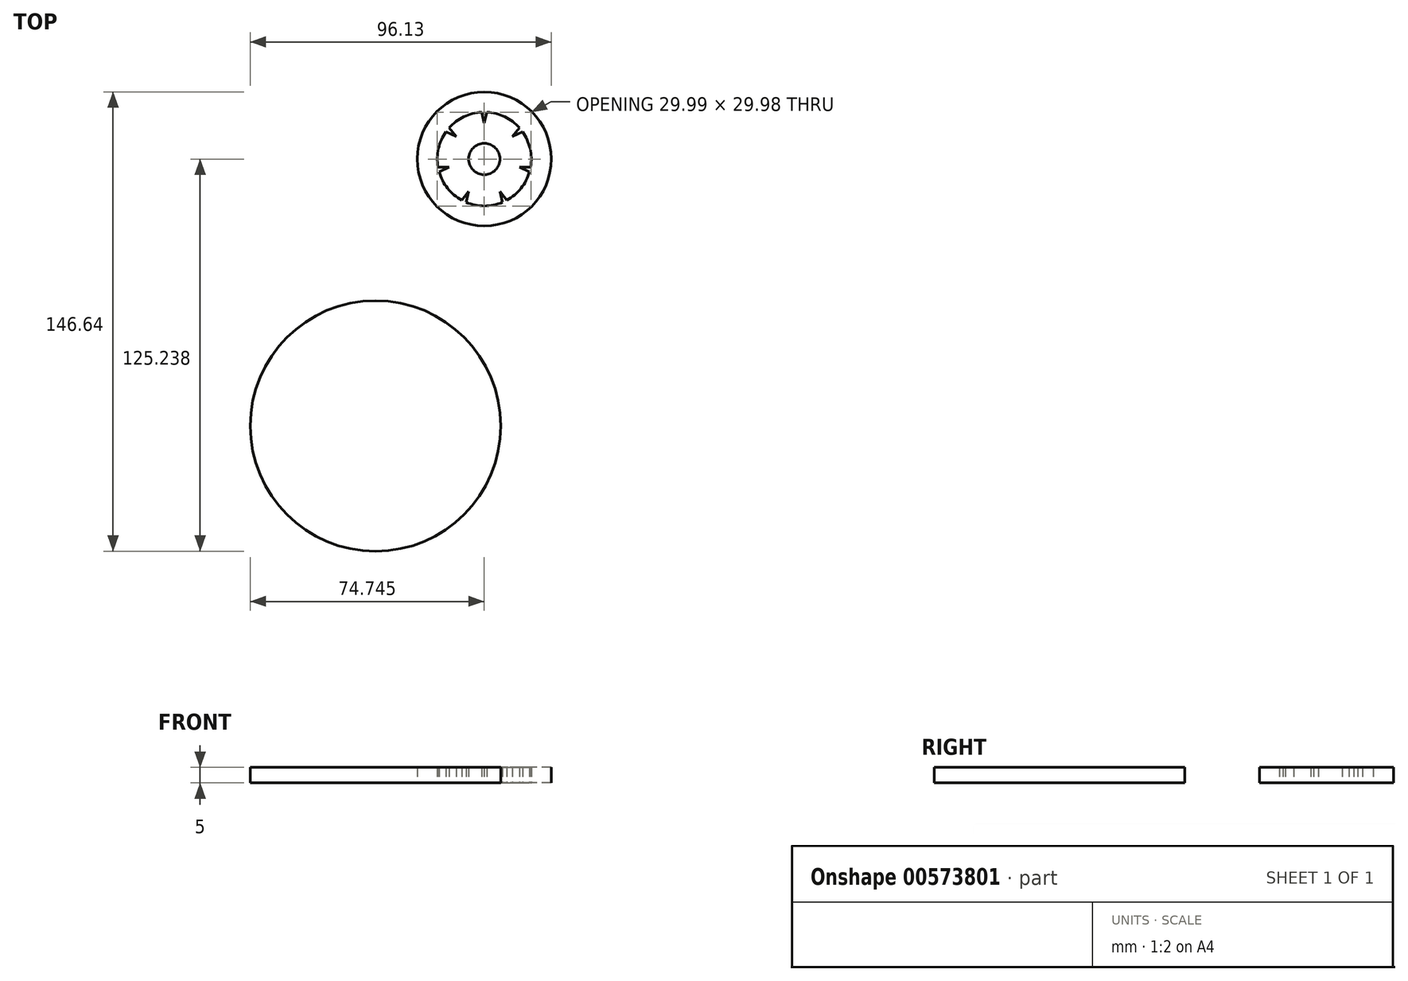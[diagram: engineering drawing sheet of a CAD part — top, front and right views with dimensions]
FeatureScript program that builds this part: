
annotation { "Feature Type Name" : "Feature", "Feature Type Description" : "" }
export const myFeature = defineFeature(function(context is Context, id is Id, definition is map)
    precondition{}
    {
        {
            var Q0;
            Q0=qCreatedBy(makeId("Top.planeOp"),FACE);
            var sketch = newSketch(context, id + "F0", { "sketchPlane" : qUnion([Q0])});
            skLineSegment(sketch, "E0.0", {"start": v(-11.35, 1.25) * mm, "end": v(-21.35, 1.25) * mm});
            skLineSegment(sketch, "E0.1", {"start": v(-21.35, 1.25) * mm, "end": v(-26.35, 9.91) * mm});
            skLineSegment(sketch, "E0.2", {"start": v(-26.35, 9.91) * mm, "end": v(-21.35, 18.57) * mm});
            skLineSegment(sketch, "E0.3", {"start": v(-21.35, 18.57) * mm, "end": v(-11.35, 18.57) * mm});
            skLineSegment(sketch, "E0.4", {"start": v(-11.35, 18.57) * mm, "end": v(-6.35, 9.91) * mm});
            skLineSegment(sketch, "E0.5", {"start": v(-6.35, 9.91) * mm, "end": v(-11.35, 1.25) * mm});
            skPoint(sketch, "E0.0.midPoint", {"position": v(-16.35, 1.25) * mm});
            skLineSegment(sketch, "E1", {"start": v(-21.35, 1.25) * mm, "end": v(-11.35, 1.25) * mm});
            skLineSegment(sketch, "E2", {"start": v(-11.35, 1.25) * mm, "end": v(-6.35, 9.91) * mm});
            skLineSegment(sketch, "E3", {"start": v(-6.35, 9.91) * mm, "end": v(-11.35, 18.57) * mm});
            skLineSegment(sketch, "E4", {"start": v(-11.35, 18.57) * mm, "end": v(-21.35, 18.57) * mm});
            skLineSegment(sketch, "E5", {"start": v(-21.35, 18.57) * mm, "end": v(-26.35, 9.91) * mm});
            skLineSegment(sketch, "E6", {"start": v(-26.35, 9.91) * mm, "end": v(-21.35, 1.25) * mm});
            skLineSegment(sketch, "E7.MirrorCS", {"start": v(-6.35, 27.23) * mm, "end": v(-11.35, 35.9) * mm});
            skLineSegment(sketch, "E8.MirrorCS", {"start": v(-21.35, 35.9) * mm, "end": v(-26.35, 27.23) * mm});
            skLineSegment(sketch, "E9.MirrorCS", {"start": v(-26.35, 27.23) * mm, "end": v(-21.35, 18.57) * mm});
            skLineSegment(sketch, "E10.MirrorCS", {"start": v(-11.35, 35.9) * mm, "end": v(-6.35, 27.23) * mm});
            skLineSegment(sketch, "E11.MirrorCS", {"start": v(-11.35, 35.9) * mm, "end": v(-21.35, 35.9) * mm});
            skLineSegment(sketch, "E12.MirrorCS", {"start": v(-11.35, 18.57) * mm, "end": v(-6.35, 27.23) * mm});
            skLineSegment(sketch, "E13.MirrorCS", {"start": v(-21.35, 35.9) * mm, "end": v(-11.35, 35.9) * mm});
            skLineSegment(sketch, "E14.MirrorCS", {"start": v(-6.35, 27.23) * mm, "end": v(-11.35, 18.57) * mm});
            skLineSegment(sketch, "E15.MirrorCS", {"start": v(-26.35, 27.23) * mm, "end": v(-21.35, 35.9) * mm});
            skLineSegment(sketch, "E16.MirrorCS", {"start": v(-21.35, 18.57) * mm, "end": v(-26.35, 27.23) * mm});
            skPoint(sketch, "E17.MirrorP", {"position": v(-16.35, 35.9) * mm});
            skLineSegment(sketch, "E18.MirrorCS", {"start": v(-6.35, 9.91) * mm, "end": v(3.65, 9.91) * mm});
            skLineSegment(sketch, "E19.MirrorCS", {"start": v(3.65, 9.91) * mm, "end": v(8.65, 18.57) * mm});
            skLineSegment(sketch, "E20.MirrorCS", {"start": v(8.65, 18.57) * mm, "end": v(3.65, 27.23) * mm});
            skLineSegment(sketch, "E21.MirrorCS", {"start": v(3.65, 27.23) * mm, "end": v(-6.35, 27.23) * mm});
            skLineSegment(sketch, "E22.MirrorCS", {"start": v(3.65, 9.91) * mm, "end": v(-6.35, 9.91) * mm});
            skPoint(sketch, "E23.MirrorP", {"position": v(6.15, 14.24) * mm});
            skLineSegment(sketch, "E24.MirrorCS", {"start": v(-6.35, 27.23) * mm, "end": v(3.65, 27.23) * mm});
            skLineSegment(sketch, "E25.MirrorCS", {"start": v(8.65, 18.57) * mm, "end": v(3.65, 9.91) * mm});
            skLineSegment(sketch, "E26.MirrorCS", {"start": v(3.65, 27.23) * mm, "end": v(8.65, 18.57) * mm});
            skLineSegment(sketch, "E27.MirrorCS", {"start": v(8.65, 1.25) * mm, "end": v(3.65, 9.91) * mm});
            skLineSegment(sketch, "E28.MirrorCS", {"start": v(3.65, -7.4) * mm, "end": v(8.65, 1.25) * mm});
            skLineSegment(sketch, "E29.MirrorCS", {"start": v(-6.35, -7.4) * mm, "end": v(3.65, -7.4) * mm});
            skLineSegment(sketch, "E30.MirrorCS", {"start": v(-11.35, 1.25) * mm, "end": v(-6.35, -7.4) * mm});
            skLineSegment(sketch, "E31.MirrorCS", {"start": v(3.65, 9.91) * mm, "end": v(8.65, 1.25) * mm});
            skPoint(sketch, "E32.MirrorP", {"position": v(-8.85, -3.08) * mm});
            skLineSegment(sketch, "E33.MirrorCS", {"start": v(3.65, -7.4) * mm, "end": v(-6.35, -7.4) * mm});
            skLineSegment(sketch, "E34.MirrorCS", {"start": v(-6.35, -7.4) * mm, "end": v(-11.35, 1.25) * mm});
            skLineSegment(sketch, "E35.MirrorCS", {"start": v(8.65, 1.25) * mm, "end": v(3.65, -7.4) * mm});
            skLineSegment(sketch, "E36.MirrorCS", {"start": v(-11.35, -16.07) * mm, "end": v(-6.35, -7.4) * mm});
            skLineSegment(sketch, "E37.MirrorCS", {"start": v(-6.35, -7.4) * mm, "end": v(-11.35, -16.07) * mm});
            skLineSegment(sketch, "E38.MirrorCS", {"start": v(-21.35, -16.07) * mm, "end": v(-11.35, -16.07) * mm});
            skLineSegment(sketch, "E39.MirrorCS", {"start": v(-21.35, 1.25) * mm, "end": v(-26.35, -7.4) * mm});
            skLineSegment(sketch, "E40.MirrorCS", {"start": v(-26.35, -7.4) * mm, "end": v(-21.35, -16.07) * mm});
            skLineSegment(sketch, "E41.MirrorCS", {"start": v(-11.35, -16.07) * mm, "end": v(-21.35, -16.07) * mm});
            skLineSegment(sketch, "E42.MirrorCS", {"start": v(-26.35, -7.4) * mm, "end": v(-21.35, 1.25) * mm});
            skLineSegment(sketch, "E43.MirrorCS", {"start": v(-21.35, -16.07) * mm, "end": v(-26.35, -7.4) * mm});
            skLineSegment(sketch, "E44.MirrorCS", {"start": v(-36.35, -7.4) * mm, "end": v(-26.35, -7.4) * mm});
            skLineSegment(sketch, "E45.MirrorCS", {"start": v(-41.35, 1.25) * mm, "end": v(-36.35, -7.4) * mm});
            skLineSegment(sketch, "E46.MirrorCS", {"start": v(-36.35, -7.4) * mm, "end": v(-41.35, 1.25) * mm});
            skLineSegment(sketch, "E47.MirrorCS", {"start": v(-26.35, -7.4) * mm, "end": v(-36.35, -7.4) * mm});
            skLineSegment(sketch, "E48.MirrorCS", {"start": v(-36.35, 9.91) * mm, "end": v(-41.35, 1.25) * mm});
            skLineSegment(sketch, "E49.MirrorCS", {"start": v(-41.35, 1.25) * mm, "end": v(-36.35, 9.91) * mm});
            skLineSegment(sketch, "E50.MirrorCS", {"start": v(-26.35, 9.91) * mm, "end": v(-36.35, 9.91) * mm});
            skLineSegment(sketch, "E51.MirrorCS", {"start": v(-36.35, 9.91) * mm, "end": v(-26.35, 9.91) * mm});
            skLineSegment(sketch, "E52.MirrorCS", {"start": v(-26.35, 27.23) * mm, "end": v(-36.35, 27.23) * mm});
            skLineSegment(sketch, "E53.MirrorCS", {"start": v(-36.35, 27.23) * mm, "end": v(-41.35, 18.57) * mm});
            skLineSegment(sketch, "E54.MirrorCS", {"start": v(-41.35, 18.57) * mm, "end": v(-36.35, 9.91) * mm});
            skLineSegment(sketch, "E55.MirrorCS", {"start": v(-41.35, 18.57) * mm, "end": v(-36.35, 27.23) * mm});
            skLineSegment(sketch, "E56.MirrorCS", {"start": v(-36.35, 27.23) * mm, "end": v(-26.35, 27.23) * mm});
            skPoint(sketch, "E57.MirrorP", {"position": v(-38.85, 14.24) * mm});
            skLineSegment(sketch, "E58.MirrorCS", {"start": v(-36.35, 9.91) * mm, "end": v(-41.35, 18.57) * mm});
            skLineSegment(sketch, "E59.MirrorCS", {"start": v(-26.35, 44.55) * mm, "end": v(-36.35, 44.55) * mm});
            skLineSegment(sketch, "E60.MirrorCS", {"start": v(-41.35, 35.9) * mm, "end": v(-36.35, 27.23) * mm});
            skLineSegment(sketch, "E61.MirrorCS", {"start": v(-36.35, 44.55) * mm, "end": v(-26.35, 44.55) * mm});
            skLineSegment(sketch, "E62.MirrorCS", {"start": v(-26.35, 44.55) * mm, "end": v(-21.35, 35.9) * mm});
            skLineSegment(sketch, "E63.MirrorCS", {"start": v(-36.35, 44.55) * mm, "end": v(-41.35, 35.9) * mm});
            skLineSegment(sketch, "E64.MirrorCS", {"start": v(-36.35, 27.23) * mm, "end": v(-41.35, 35.9) * mm});
            skLineSegment(sketch, "E65.MirrorCS", {"start": v(-21.35, 35.9) * mm, "end": v(-26.35, 44.55) * mm});
            skPoint(sketch, "E66.MirrorP", {"position": v(-38.85, 40.22) * mm});
            skLineSegment(sketch, "E67.MirrorCS", {"start": v(-41.35, 35.9) * mm, "end": v(-36.35, 44.55) * mm});
            skLineSegment(sketch, "E68.MirrorCS", {"start": v(-56.35, 9.91) * mm, "end": v(-51.35, 18.57) * mm});
            skLineSegment(sketch, "E69.MirrorCS", {"start": v(-41.35, 1.25) * mm, "end": v(-51.35, 1.25) * mm});
            skLineSegment(sketch, "E70.MirrorCS", {"start": v(-56.35, 9.91) * mm, "end": v(-51.35, 1.25) * mm});
            skLineSegment(sketch, "E71.MirrorCS", {"start": v(-51.35, 1.25) * mm, "end": v(-56.35, 9.91) * mm});
            skLineSegment(sketch, "E72.MirrorCS", {"start": v(-51.35, 18.57) * mm, "end": v(-56.35, 9.91) * mm});
            skLineSegment(sketch, "E73.MirrorCS", {"start": v(-51.35, 18.57) * mm, "end": v(-41.35, 18.57) * mm});
            skLineSegment(sketch, "E74.MirrorCS", {"start": v(-41.35, 18.57) * mm, "end": v(-51.35, 18.57) * mm});
            skLineSegment(sketch, "E75.MirrorCS", {"start": v(-51.35, 1.25) * mm, "end": v(-41.35, 1.25) * mm});
            skLineSegment(sketch, "E76.MirrorCS", {"start": v(-6.35, 44.55) * mm, "end": v(3.65, 44.55) * mm});
            skLineSegment(sketch, "E77.MirrorCS", {"start": v(3.65, 44.55) * mm, "end": v(-6.35, 44.55) * mm});
            skLineSegment(sketch, "E78.MirrorCS", {"start": v(8.65, 35.9) * mm, "end": v(3.65, 44.55) * mm});
            skLineSegment(sketch, "E79.MirrorCS", {"start": v(3.65, 44.55) * mm, "end": v(8.65, 35.9) * mm});
            skLineSegment(sketch, "E80.MirrorCS", {"start": v(8.65, 35.9) * mm, "end": v(3.65, 27.23) * mm});
            skLineSegment(sketch, "E81.MirrorCS", {"start": v(3.65, 27.23) * mm, "end": v(8.65, 35.9) * mm});
            skLineSegment(sketch, "E82.MirrorCS", {"start": v(-6.35, 44.55) * mm, "end": v(-11.35, 35.9) * mm});
            skLineSegment(sketch, "E83.MirrorCS", {"start": v(-11.35, 35.9) * mm, "end": v(-6.35, 44.55) * mm});
            skPoint(sketch, "E84.MirrorP", {"position": v(-8.85, 40.22) * mm});
            skLineSegment(sketch, "E85.MirrorCS", {"start": v(23.65, 9.91) * mm, "end": v(18.65, 18.57) * mm});
            skLineSegment(sketch, "E86.MirrorCS", {"start": v(18.65, 1.25) * mm, "end": v(23.65, 9.91) * mm});
            skLineSegment(sketch, "E87.MirrorCS", {"start": v(18.65, 18.57) * mm, "end": v(23.65, 9.91) * mm});
            skLineSegment(sketch, "E88.MirrorCS", {"start": v(23.65, 9.91) * mm, "end": v(18.65, 1.25) * mm});
            skLineSegment(sketch, "E89.MirrorCS", {"start": v(18.65, 1.25) * mm, "end": v(8.65, 1.25) * mm});
            skLineSegment(sketch, "E90.MirrorCS", {"start": v(18.65, 18.57) * mm, "end": v(8.65, 18.57) * mm});
            skLineSegment(sketch, "E91.MirrorCS", {"start": v(8.65, 1.25) * mm, "end": v(18.65, 1.25) * mm});
            skLineSegment(sketch, "E92.MirrorCS", {"start": v(8.65, 18.57) * mm, "end": v(18.65, 18.57) * mm});
            skLineSegment(sketch, "E93.MirrorCS", {"start": v(8.65, -16.07) * mm, "end": v(3.65, -24.73) * mm});
            skLineSegment(sketch, "E94.MirrorCS", {"start": v(3.65, -24.73) * mm, "end": v(8.65, -16.07) * mm});
            skLineSegment(sketch, "E95.MirrorCS", {"start": v(3.65, -24.73) * mm, "end": v(-6.35, -24.73) * mm});
            skLineSegment(sketch, "E96.MirrorCS", {"start": v(-6.35, -24.73) * mm, "end": v(3.65, -24.73) * mm});
            skLineSegment(sketch, "E97.MirrorCS", {"start": v(-6.35, -24.73) * mm, "end": v(-11.35, -16.07) * mm});
            skLineSegment(sketch, "E98.MirrorCS", {"start": v(-11.35, -16.07) * mm, "end": v(-6.35, -24.73) * mm});
            skPoint(sketch, "E99.MirrorP", {"position": v(-16.35, -16.07) * mm});
            skLineSegment(sketch, "E100.MirrorCS", {"start": v(8.65, -16.07) * mm, "end": v(3.65, -7.4) * mm});
            skPoint(sketch, "E101.MirrorP", {"position": v(-8.85, -11.74) * mm});
            skLineSegment(sketch, "E102.MirrorCS", {"start": v(3.65, -7.4) * mm, "end": v(8.65, -16.07) * mm});
            skLineSegment(sketch, "E103.MirrorCS", {"start": v(-26.35, -24.73) * mm, "end": v(-36.35, -24.73) * mm});
            skLineSegment(sketch, "E104.MirrorCS", {"start": v(-36.35, -24.73) * mm, "end": v(-26.35, -24.73) * mm});
            skLineSegment(sketch, "E105.MirrorCS", {"start": v(-36.35, -24.73) * mm, "end": v(-41.35, -16.07) * mm});
            skLineSegment(sketch, "E106.MirrorCS", {"start": v(-41.35, -16.07) * mm, "end": v(-36.35, -24.73) * mm});
            skLineSegment(sketch, "E107.MirrorCS", {"start": v(-41.35, -16.07) * mm, "end": v(-36.35, -7.4) * mm});
            skLineSegment(sketch, "E108.MirrorCS", {"start": v(-26.35, -24.73) * mm, "end": v(-21.35, -16.07) * mm});
            skPoint(sketch, "E109.MirrorP", {"position": v(-38.85, -11.74) * mm});
            skLineSegment(sketch, "E110.MirrorCS", {"start": v(-21.35, -16.07) * mm, "end": v(-26.35, -24.73) * mm});
            skPoint(sketch, "E111.MirrorP", {"position": v(-23.85, -20.4) * mm});
            skLineSegment(sketch, "E112.MirrorCS", {"start": v(-36.35, -7.4) * mm, "end": v(-41.35, -16.07) * mm});
            skPoint(sketch, "E113.MirrorP", {"position": v(-38.85, -20.4) * mm});
            skPoint(sketch, "E114.MirrorP", {"position": v(-31.35, -24.73) * mm});
            skLineSegment(sketch, "E115.0", {"start": v(107.66, 12.57) * mm, "end": v(97.66, 12.57) * mm});
            skLineSegment(sketch, "E115.1", {"start": v(97.66, 12.57) * mm, "end": v(91.43, 20.38) * mm});
            skLineSegment(sketch, "E115.2", {"start": v(91.43, 20.38) * mm, "end": v(93.66, 30.13) * mm});
            skLineSegment(sketch, "E115.3", {"start": v(93.66, 30.13) * mm, "end": v(102.66, 34.47) * mm});
            skLineSegment(sketch, "E115.4", {"start": v(102.66, 34.47) * mm, "end": v(111.67, 30.13) * mm});
            skLineSegment(sketch, "E115.5", {"start": v(111.67, 30.13) * mm, "end": v(113.9, 20.38) * mm});
            skLineSegment(sketch, "E115.6", {"start": v(113.9, 20.38) * mm, "end": v(107.66, 12.57) * mm});
            skPoint(sketch, "E115.0.midPoint", {"position": v(102.66, 12.57) * mm});
            skLineSegment(sketch, "E116", {"start": v(97.66, 12.57) * mm, "end": v(107.66, 12.57) * mm});
            skLineSegment(sketch, "E117", {"start": v(107.66, 12.57) * mm, "end": v(113.9, 20.38) * mm});
            skLineSegment(sketch, "E118", {"start": v(113.9, 20.38) * mm, "end": v(111.67, 30.13) * mm});
            skLineSegment(sketch, "E119", {"start": v(111.67, 30.13) * mm, "end": v(102.66, 34.47) * mm});
            skLineSegment(sketch, "E120", {"start": v(102.66, 34.47) * mm, "end": v(93.66, 30.13) * mm});
            skLineSegment(sketch, "E121", {"start": v(93.66, 30.13) * mm, "end": v(91.43, 20.38) * mm});
            skLineSegment(sketch, "E122", {"start": v(91.43, 20.38) * mm, "end": v(97.66, 12.57) * mm});
            skLineSegment(sketch, "E123.MirrorCS", {"start": v(106.67, 52.04) * mm, "end": v(116.67, 52.04) * mm});
            skLineSegment(sketch, "E124.MirrorCS", {"start": v(100.44, 44.22) * mm, "end": v(106.67, 52.04) * mm});
            skLineSegment(sketch, "E125.MirrorCS", {"start": v(116.67, 52.04) * mm, "end": v(122.9, 44.22) * mm});
            skLineSegment(sketch, "E126.MirrorCS", {"start": v(120.68, 34.47) * mm, "end": v(111.67, 30.13) * mm});
            skLineSegment(sketch, "E127.MirrorCS", {"start": v(122.9, 44.22) * mm, "end": v(120.68, 34.47) * mm});
            skLineSegment(sketch, "E128.MirrorCS", {"start": v(102.66, 34.47) * mm, "end": v(100.44, 44.22) * mm});
            skLineSegment(sketch, "E129.MirrorCS", {"start": v(116.67, 52.04) * mm, "end": v(106.67, 52.04) * mm});
            skLineSegment(sketch, "E130.MirrorCS", {"start": v(106.67, 52.04) * mm, "end": v(100.44, 44.22) * mm});
            skLineSegment(sketch, "E131.MirrorCS", {"start": v(100.44, 44.22) * mm, "end": v(102.66, 34.47) * mm});
            skLineSegment(sketch, "E132.MirrorCS", {"start": v(111.67, 30.13) * mm, "end": v(120.68, 34.47) * mm});
            skLineSegment(sketch, "E133.MirrorCS", {"start": v(122.9, 44.22) * mm, "end": v(116.67, 52.04) * mm});
            skLineSegment(sketch, "E134.MirrorCS", {"start": v(120.68, 34.47) * mm, "end": v(122.9, 44.22) * mm});
            skPoint(sketch, "E135.MirrorP", {"position": v(119.8, 48.13) * mm});
            skLineSegment(sketch, "E136.MirrorCS", {"start": v(111.67, 30.13) * mm, "end": v(117.9, 37.95) * mm});
            skLineSegment(sketch, "E137.MirrorCS", {"start": v(131.92, 20.38) * mm, "end": v(122.9, 16.05) * mm});
            skLineSegment(sketch, "E138.MirrorCS", {"start": v(134.14, 30.13) * mm, "end": v(131.92, 20.38) * mm});
            skLineSegment(sketch, "E139.MirrorCS", {"start": v(127.9, 37.95) * mm, "end": v(134.14, 30.13) * mm});
            skLineSegment(sketch, "E140.MirrorCS", {"start": v(122.9, 16.05) * mm, "end": v(113.9, 20.38) * mm});
            skLineSegment(sketch, "E141.MirrorCS", {"start": v(117.9, 37.95) * mm, "end": v(127.9, 37.95) * mm});
            skLineSegment(sketch, "E142.MirrorCS", {"start": v(131.92, 20.38) * mm, "end": v(134.14, 30.13) * mm});
            skLineSegment(sketch, "E143.MirrorCS", {"start": v(134.14, 30.13) * mm, "end": v(127.9, 37.95) * mm});
            skLineSegment(sketch, "E144.MirrorCS", {"start": v(127.9, 37.95) * mm, "end": v(117.9, 37.95) * mm});
            skPoint(sketch, "E145.MirrorP", {"position": v(127.41, 18.21) * mm});
            skLineSegment(sketch, "E146.MirrorCS", {"start": v(117.9, 37.95) * mm, "end": v(111.67, 30.13) * mm});
            skLineSegment(sketch, "E147.MirrorCS", {"start": v(113.9, 20.38) * mm, "end": v(122.9, 16.05) * mm});
            skLineSegment(sketch, "E148.MirrorCS", {"start": v(122.9, 16.05) * mm, "end": v(131.92, 20.38) * mm});
            skLineSegment(sketch, "E149.MirrorCS", {"start": v(123.9, 20.38) * mm, "end": v(130.13, 12.57) * mm});
            skLineSegment(sketch, "E150.MirrorCS", {"start": v(113.9, 20.38) * mm, "end": v(123.9, 20.38) * mm});
            skLineSegment(sketch, "E151.MirrorCS", {"start": v(127.9, 2.82) * mm, "end": v(118.9, -1.52) * mm});
            skLineSegment(sketch, "E152.MirrorCS", {"start": v(130.13, 12.57) * mm, "end": v(127.9, 2.82) * mm});
            skLineSegment(sketch, "E153.MirrorCS", {"start": v(109.89, 2.82) * mm, "end": v(107.66, 12.57) * mm});
            skLineSegment(sketch, "E154.MirrorCS", {"start": v(118.9, -1.52) * mm, "end": v(109.89, 2.82) * mm});
            skLineSegment(sketch, "E155.MirrorCS", {"start": v(107.66, 12.57) * mm, "end": v(109.89, 2.82) * mm});
            skPoint(sketch, "E156.MirrorP", {"position": v(108.78, 7.7) * mm});
            skLineSegment(sketch, "E157.MirrorCS", {"start": v(123.9, 20.38) * mm, "end": v(113.9, 20.38) * mm});
            skLineSegment(sketch, "E158.MirrorCS", {"start": v(127.9, 2.82) * mm, "end": v(130.13, 12.57) * mm});
            skLineSegment(sketch, "E159.MirrorCS", {"start": v(109.89, 2.82) * mm, "end": v(118.9, -1.52) * mm});
            skLineSegment(sketch, "E160.MirrorCS", {"start": v(130.13, 12.57) * mm, "end": v(123.9, 20.38) * mm});
            skLineSegment(sketch, "E161.MirrorCS", {"start": v(118.9, -1.52) * mm, "end": v(127.9, 2.82) * mm});
            skLineSegment(sketch, "E162.MirrorCS", {"start": v(107.66, 12.57) * mm, "end": v(113.9, 4.75) * mm});
            skLineSegment(sketch, "E163.MirrorCS", {"start": v(111.67, -5) * mm, "end": v(102.66, -9.34) * mm});
            skLineSegment(sketch, "E164.MirrorCS", {"start": v(113.9, 4.75) * mm, "end": v(111.67, -5) * mm});
            skLineSegment(sketch, "E165.MirrorCS", {"start": v(91.43, 4.75) * mm, "end": v(97.66, 12.57) * mm});
            skLineSegment(sketch, "E166.MirrorCS", {"start": v(93.66, -5) * mm, "end": v(91.43, 4.75) * mm});
            skLineSegment(sketch, "E167.MirrorCS", {"start": v(102.66, -9.34) * mm, "end": v(93.66, -5) * mm});
            skLineSegment(sketch, "E168.MirrorCS", {"start": v(97.66, 12.57) * mm, "end": v(91.43, 4.75) * mm});
            skLineSegment(sketch, "E169.MirrorCS", {"start": v(91.43, 4.75) * mm, "end": v(93.66, -5) * mm});
            skLineSegment(sketch, "E170.MirrorCS", {"start": v(93.66, -5) * mm, "end": v(102.66, -9.34) * mm});
            skLineSegment(sketch, "E171.MirrorCS", {"start": v(102.66, -9.34) * mm, "end": v(111.67, -5) * mm});
            skLineSegment(sketch, "E172.MirrorCS", {"start": v(111.67, -5) * mm, "end": v(113.9, 4.75) * mm});
            skLineSegment(sketch, "E173.MirrorCS", {"start": v(113.9, 4.75) * mm, "end": v(107.66, 12.57) * mm});
            skLineSegment(sketch, "E174.MirrorCS", {"start": v(97.66, 12.57) * mm, "end": v(95.44, 2.82) * mm});
            skLineSegment(sketch, "E175.MirrorCS", {"start": v(77.42, 2.82) * mm, "end": v(75.2, 12.57) * mm});
            skLineSegment(sketch, "E176.MirrorCS", {"start": v(86.43, -1.52) * mm, "end": v(77.42, 2.82) * mm});
            skLineSegment(sketch, "E177.MirrorCS", {"start": v(95.44, 2.82) * mm, "end": v(86.43, -1.52) * mm});
            skLineSegment(sketch, "E178.MirrorCS", {"start": v(81.43, 20.38) * mm, "end": v(91.43, 20.38) * mm});
            skLineSegment(sketch, "E179.MirrorCS", {"start": v(75.2, 12.57) * mm, "end": v(81.43, 20.38) * mm});
            skPoint(sketch, "E180.MirrorP", {"position": v(96.55, 7.7) * mm});
            skLineSegment(sketch, "E181.MirrorCS", {"start": v(86.43, -1.52) * mm, "end": v(95.44, 2.82) * mm});
            skLineSegment(sketch, "E182.MirrorCS", {"start": v(77.42, 2.82) * mm, "end": v(86.43, -1.52) * mm});
            skLineSegment(sketch, "E183.MirrorCS", {"start": v(95.44, 2.82) * mm, "end": v(97.66, 12.57) * mm});
            skLineSegment(sketch, "E184.MirrorCS", {"start": v(75.2, 12.57) * mm, "end": v(77.42, 2.82) * mm});
            skLineSegment(sketch, "E185.MirrorCS", {"start": v(81.43, 20.38) * mm, "end": v(75.2, 12.57) * mm});
            skLineSegment(sketch, "E186.MirrorCS", {"start": v(91.43, 20.38) * mm, "end": v(81.43, 20.38) * mm});
            skLineSegment(sketch, "E187.MirrorCS", {"start": v(82.42, 44.22) * mm, "end": v(88.66, 52.04) * mm});
            skLineSegment(sketch, "E188.MirrorCS", {"start": v(88.66, 52.04) * mm, "end": v(98.66, 52.04) * mm});
            skLineSegment(sketch, "E189.MirrorCS", {"start": v(84.65, 34.47) * mm, "end": v(82.42, 44.22) * mm});
            skLineSegment(sketch, "E190.MirrorCS", {"start": v(104.89, 44.22) * mm, "end": v(102.66, 34.47) * mm});
            skLineSegment(sketch, "E191.MirrorCS", {"start": v(98.66, 52.04) * mm, "end": v(104.89, 44.22) * mm});
            skLineSegment(sketch, "E192.MirrorCS", {"start": v(82.42, 44.22) * mm, "end": v(84.65, 34.47) * mm});
            skPoint(sketch, "E193.MirrorP", {"position": v(85.54, 48.13) * mm});
            skLineSegment(sketch, "E194.MirrorCS", {"start": v(93.66, 30.13) * mm, "end": v(84.65, 34.47) * mm});
            skLineSegment(sketch, "E195.MirrorCS", {"start": v(98.66, 52.04) * mm, "end": v(88.66, 52.04) * mm});
            skLineSegment(sketch, "E196.MirrorCS", {"start": v(84.65, 34.47) * mm, "end": v(93.66, 30.13) * mm});
            skLineSegment(sketch, "E197.MirrorCS", {"start": v(104.89, 44.22) * mm, "end": v(98.66, 52.04) * mm});
            skLineSegment(sketch, "E198.MirrorCS", {"start": v(102.66, 34.47) * mm, "end": v(104.89, 44.22) * mm});
            skLineSegment(sketch, "E199.MirrorCS", {"start": v(88.66, 52.04) * mm, "end": v(82.42, 44.22) * mm});
            skLineSegment(sketch, "E200.MirrorCS", {"start": v(82.42, 16.05) * mm, "end": v(73.41, 20.38) * mm});
            skLineSegment(sketch, "E201.MirrorCS", {"start": v(73.41, 20.38) * mm, "end": v(82.42, 16.05) * mm});
            skLineSegment(sketch, "E202.MirrorCS", {"start": v(87.42, 37.95) * mm, "end": v(93.66, 30.13) * mm});
            skLineSegment(sketch, "E203.MirrorCS", {"start": v(77.42, 37.95) * mm, "end": v(87.42, 37.95) * mm});
            skLineSegment(sketch, "E204.MirrorCS", {"start": v(71.19, 30.13) * mm, "end": v(77.42, 37.95) * mm});
            skLineSegment(sketch, "E205.MirrorCS", {"start": v(73.41, 20.38) * mm, "end": v(71.19, 30.13) * mm});
            skLineSegment(sketch, "E206.MirrorCS", {"start": v(91.43, 20.38) * mm, "end": v(82.42, 16.05) * mm});
            skLineSegment(sketch, "E207.MirrorCS", {"start": v(82.42, 16.05) * mm, "end": v(91.43, 20.38) * mm});
            skPoint(sketch, "E208.MirrorP", {"position": v(77.92, 18.21) * mm});
            skLineSegment(sketch, "E209.MirrorCS", {"start": v(93.66, 30.13) * mm, "end": v(87.42, 37.95) * mm});
            skLineSegment(sketch, "E210.MirrorCS", {"start": v(71.19, 30.13) * mm, "end": v(73.41, 20.38) * mm});
            skLineSegment(sketch, "E211.MirrorCS", {"start": v(77.42, 37.95) * mm, "end": v(71.19, 30.13) * mm});
            skLineSegment(sketch, "E212.MirrorCS", {"start": v(87.42, 37.95) * mm, "end": v(77.42, 37.95) * mm});
            skCircle(sketch, "E213", {"center": v(67.92, -62.3) * mm, "radius": 40 * mm});
            skLineSegment(sketch, "E214", {"start": v(93.66, 30.13) * mm, "end": v(110.78, 16.47) * mm});
            skLineSegment(sketch, "E215", {"start": v(107.66, 12.57) * mm, "end": v(98.16, 32.3) * mm});
            skLineSegment(sketch, "E216", {"start": v(91.43, 20.38) * mm, "end": v(112.79, 25.26) * mm});
            skLineSegment(sketch, "E217", {"start": v(97.66, 12.57) * mm, "end": v(107.17, 32.3) * mm});
            skLineSegment(sketch, "E218", {"start": v(111.67, 30.13) * mm, "end": v(94.55, 16.47) * mm});
            skLineSegment(sketch, "E219", {"start": v(113.9, 20.38) * mm, "end": v(92.54, 25.26) * mm});
            skLineSegment(sketch, "E220", {"start": v(102.66, 34.47) * mm, "end": v(102.66, 12.57) * mm});
            skCircle(sketch, "E221", {"center": v(102.66, 22.95) * mm, "radius": 15 * mm});
            skCircle(sketch, "E222", {"center": v(102.66, 22.95) * mm, "radius": 21.39 * mm});
            skCircle(sketch, "E223", {"center": v(102.66, 22.95) * mm, "radius": 29.37 * mm});
            skCircle(sketch, "E224", {"center": v(102.66, 22.95) * mm, "radius": 5 * mm});
            skSolve(sketch);
        }
        {
            var Q0;
            Q0=makeQuery(id+"F0.imprint","IMPRINT",FACE,{"disambiguationData":[TD([[makeQuery(id+"F0.imprint","IMPRINT",EDGE,{"derivedFrom":sQuery(id+"F0.wireOp",EDGE,"E213")}),1.0]])]});
            var Q1;
            {var subQ0=sQuery(id+"F0.wireOp",EDGE,"E129.MirrorCS");Q1=makeQuery(id+"F0.imprint","IMPRINT",FACE,{"disambiguationData":[TD([[makeQuery(id+"F0.imprint","IMPRINT",EDGE,{"derivedFrom":subQ0}),1.0]])]});}
            var Q2;
            {var subQ0=sQuery(id+"F0.wireOp",EDGE,"E142.MirrorCS");Q2=makeQuery(id+"F0.imprint","IMPRINT",FACE,{"disambiguationData":[TD([[makeQuery(id+"F0.imprint","IMPRINT",EDGE,{"derivedFrom":subQ0}),1.0]])]});}
            var Q3;
            {var subQ0=sQuery(id+"F0.wireOp",EDGE,"E158.MirrorCS");Q3=makeQuery(id+"F0.imprint","IMPRINT",FACE,{"disambiguationData":[TD([[makeQuery(id+"F0.imprint","IMPRINT",EDGE,{"derivedFrom":subQ0}),1.0]])]});}
            var Q4;
            {var subQ0=sQuery(id+"F0.wireOp",EDGE,"E170.MirrorCS");Q4=makeQuery(id+"F0.imprint","IMPRINT",FACE,{"disambiguationData":[TD([[makeQuery(id+"F0.imprint","IMPRINT",EDGE,{"derivedFrom":subQ0}),1.0]])]});}
            var Q5;
            {var subQ0=sQuery(id+"F0.wireOp",EDGE,"E182.MirrorCS");Q5=makeQuery(id+"F0.imprint","IMPRINT",FACE,{"disambiguationData":[TD([[makeQuery(id+"F0.imprint","IMPRINT",EDGE,{"derivedFrom":subQ0}),1.0]])]});}
            var Q6;
            {var subQ0=sQuery(id+"F0.wireOp",EDGE,"E195.MirrorCS");Q6=makeQuery(id+"F0.imprint","IMPRINT",FACE,{"disambiguationData":[TD([[makeQuery(id+"F0.imprint","IMPRINT",EDGE,{"derivedFrom":subQ0}),1.0]])]});}
            var Q7;
            {var subQ0=sQuery(id+"F0.wireOp",EDGE,"E210.MirrorCS");Q7=makeQuery(id+"F0.imprint","IMPRINT",FACE,{"disambiguationData":[TD([[makeQuery(id+"F0.imprint","IMPRINT",EDGE,{"derivedFrom":subQ0}),1.0]])]});}
            var Q8;
            Q8=makeQuery(id+"F0.imprint","IMPRINT",FACE,{"disambiguationData":[TD([[makeQuery(id+"F0.imprint","IMPRINT",EDGE,{"derivedFrom":sQuery(id+"F0.wireOp",EDGE,"E52.MirrorCS")}),-1.0]])]});
            var Q9;
            Q9=makeQuery(id+"F0.imprint","IMPRINT",FACE,{"disambiguationData":[TD([[makeQuery(id+"F0.imprint","IMPRINT",EDGE,{"derivedFrom":sQuery(id+"F0.wireOp",EDGE,"E49.MirrorCS")}),1.0]])]});
            var Q10;
            Q10=makeQuery(id+"F0.imprint","IMPRINT",FACE,{"disambiguationData":[TD([[makeQuery(id+"F0.imprint","IMPRINT",EDGE,{"derivedFrom":sQuery(id+"F0.wireOp",EDGE,"E7.MirrorCS")}),-1.0]])]});
            var Q11;
            Q11=makeQuery(id+"F0.imprint","IMPRINT",FACE,{"disambiguationData":[TD([[makeQuery(id+"F0.imprint","IMPRINT",EDGE,{"derivedFrom":sQuery(id+"F0.wireOp",EDGE,"E19.MirrorCS")}),-1.0]])]});
            var Q12;
            Q12=makeQuery(id+"F0.imprint","IMPRINT",FACE,{"disambiguationData":[TD([[makeQuery(id+"F0.imprint","IMPRINT",EDGE,{"derivedFrom":sQuery(id+"F0.wireOp",EDGE,"E33.MirrorCS")}),1.0]])]});
            var Q13;
            Q13=makeQuery(id+"F0.imprint","IMPRINT",FACE,{"disambiguationData":[TD([[makeQuery(id+"F0.imprint","IMPRINT",EDGE,{"derivedFrom":sQuery(id+"F0.wireOp",EDGE,"E104.MirrorCS")}),1.0]])]});
            var Q14;
            Q14=makeQuery(id+"F0.imprint","IMPRINT",FACE,{"disambiguationData":[TD([[makeQuery(id+"F0.imprint","IMPRINT",EDGE,{"derivedFrom":sQuery(id+"F0.wireOp",EDGE,"E0.3")}),1.0]])]});
            var Q15;
            Q15=makeQuery(id+"F0.imprint","IMPRINT",FACE,{"disambiguationData":[TD([[makeQuery(id+"F0.imprint","IMPRINT",EDGE,{"derivedFrom":sQuery(id+"F0.wireOp",EDGE,"E0.4")}),1.0]])]});
            var Q16;
            Q16=makeQuery(id+"F0.imprint","IMPRINT",FACE,{"disambiguationData":[TD([[makeQuery(id+"F0.imprint","IMPRINT",EDGE,{"derivedFrom":sQuery(id+"F0.wireOp",EDGE,"E2")}),-1.0]])]});
            var Q17;
            Q17=makeQuery(id+"F0.imprint","IMPRINT",FACE,{"disambiguationData":[TD([[makeQuery(id+"F0.imprint","IMPRINT",EDGE,{"derivedFrom":sQuery(id+"F0.wireOp",EDGE,"E0.0")}),1.0]])]});
            var Q18;
            Q18=makeQuery(id+"F0.imprint","IMPRINT",FACE,{"disambiguationData":[TD([[makeQuery(id+"F0.imprint","IMPRINT",EDGE,{"derivedFrom":sQuery(id+"F0.wireOp",EDGE,"E0.1")}),1.0]])]});
            var Q19;
            Q19=makeQuery(id+"F0.imprint","IMPRINT",FACE,{"disambiguationData":[TD([[makeQuery(id+"F0.imprint","IMPRINT",EDGE,{"derivedFrom":sQuery(id+"F0.wireOp",EDGE,"E0.2")}),1.0]])]});
            var Q20;
            {var subQ1=sQuery(id+"F0.wireOp",EDGE,"E197.MirrorCS");var subQ3=sQuery(id+"F0.wireOp",EDGE,"E130.MirrorCS");var subQ4=makeQuery(id+"F0.imprint","INTERSECT",VERTEX,{"derivedFrom":[subQ3,subQ1]});Q20=makeQuery(id+"F0.imprint","IMPRINT",FACE,{"disambiguationData":[TD([[makeQuery(id+"F0.imprint","IMPRINT",EDGE,{"disambiguationData":[TD([[subQ4,1.0]])],"derivedFrom":subQ3}),1.0]])]});}
            var Q21;
            {var subQ6=sQuery(id+"F0.wireOp",EDGE,"E197.MirrorCS");var subQ8=sQuery(id+"F0.wireOp",EDGE,"E130.MirrorCS");var subQ9=makeQuery(id+"F0.imprint","INTERSECT",VERTEX,{"derivedFrom":[subQ8,subQ6]});Q21=makeQuery(id+"F0.imprint","IMPRINT",FACE,{"disambiguationData":[TD([[makeQuery(id+"F0.imprint","IMPRINT",EDGE,{"disambiguationData":[TD([[subQ9,-1.0]])],"derivedFrom":subQ8}),-1.0]])]});}
            var Q22;
            {var subQ7=sQuery(id+"F0.wireOp",EDGE,"E144.MirrorCS");var subQ9=sQuery(id+"F0.wireOp",EDGE,"E134.MirrorCS");var subQ10=makeQuery(id+"F0.imprint","INTERSECT",VERTEX,{"derivedFrom":[subQ9,subQ7]});Q22=makeQuery(id+"F0.imprint","IMPRINT",FACE,{"disambiguationData":[TD([[makeQuery(id+"F0.imprint","IMPRINT",EDGE,{"disambiguationData":[TD([[subQ10,1.0]])],"derivedFrom":subQ9}),-1.0]])]});}
            var Q23;
            {var subQ6=sQuery(id+"F0.wireOp",EDGE,"E160.MirrorCS");var subQ8=sQuery(id+"F0.wireOp",EDGE,"E148.MirrorCS");var subQ9=makeQuery(id+"F0.imprint","INTERSECT",VERTEX,{"derivedFrom":[subQ8,subQ6]});Q23=makeQuery(id+"F0.imprint","IMPRINT",FACE,{"disambiguationData":[TD([[makeQuery(id+"F0.imprint","IMPRINT",EDGE,{"disambiguationData":[TD([[subQ9,1.0]])],"derivedFrom":subQ8}),-1.0]])]});}
            var Q24;
            {var subQ1=sQuery(id+"F0.wireOp",EDGE,"E172.MirrorCS");var subQ3=sQuery(id+"F0.wireOp",EDGE,"E159.MirrorCS");var subQ4=makeQuery(id+"F0.imprint","INTERSECT",VERTEX,{"derivedFrom":[subQ3,subQ1]});Q24=makeQuery(id+"F0.imprint","IMPRINT",FACE,{"disambiguationData":[TD([[makeQuery(id+"F0.imprint","IMPRINT",EDGE,{"disambiguationData":[TD([[subQ4,1.0]])],"derivedFrom":subQ3}),-1.0]])]});}
            var Q25;
            {var subQ5=sQuery(id+"F0.wireOp",EDGE,"E169.MirrorCS");var subQ7=sQuery(id+"F0.wireOp",EDGE,"E181.MirrorCS");var subQ8=makeQuery(id+"F0.imprint","INTERSECT",VERTEX,{"derivedFrom":[subQ5,subQ7]});Q25=makeQuery(id+"F0.imprint","IMPRINT",FACE,{"disambiguationData":[TD([[makeQuery(id+"F0.imprint","IMPRINT",EDGE,{"disambiguationData":[TD([[subQ8,1.0]])],"derivedFrom":subQ5}),-1.0]])]});}
            var Q26;
            {var subQ1=sQuery(id+"F0.wireOp",EDGE,"E201.MirrorCS");var subQ3=sQuery(id+"F0.wireOp",EDGE,"E185.MirrorCS");var subQ4=makeQuery(id+"F0.imprint","INTERSECT",VERTEX,{"derivedFrom":[subQ3,subQ1]});Q26=makeQuery(id+"F0.imprint","IMPRINT",FACE,{"disambiguationData":[TD([[makeQuery(id+"F0.imprint","IMPRINT",EDGE,{"disambiguationData":[TD([[subQ4,1.0]])],"derivedFrom":subQ3}),-1.0]])]});}
            var Q27;
            {var subQ1=sQuery(id+"F0.wireOp",EDGE,"E146.MirrorCS");var subQ3=sQuery(id+"F0.wireOp",EDGE,"E221");var subQ4=makeQuery(id+"F0.imprint","INTERSECT",VERTEX,{"derivedFrom":[subQ1,subQ3]});Q27=makeQuery(id+"F0.imprint","IMPRINT",FACE,{"disambiguationData":[TD([[makeQuery(id+"F0.imprint","IMPRINT",EDGE,{"disambiguationData":[TD([[subQ4,-1.0]])],"derivedFrom":subQ3}),-1.0]])]});}
            var Q28;
            {var subQ3=sQuery(id+"F0.wireOp",EDGE,"E221");var subQ5=sQuery(id+"F0.wireOp",EDGE,"E146.MirrorCS");var subQ7=makeQuery(id+"F0.imprint","INTERSECT",VERTEX,{"derivedFrom":[subQ5,subQ3]});Q28=makeQuery(id+"F0.imprint","IMPRINT",FACE,{"disambiguationData":[TD([[makeQuery(id+"F0.imprint","IMPRINT",EDGE,{"disambiguationData":[TD([[subQ7,-1.0]])],"derivedFrom":subQ3}),1.0]])]});}
            var Q29;
            {var subQ1=sQuery(id+"F0.wireOp",EDGE,"E132.MirrorCS");var subQ3=sQuery(id+"F0.wireOp",EDGE,"E221");var subQ4=makeQuery(id+"F0.imprint","INTERSECT",VERTEX,{"derivedFrom":[subQ1,subQ3]});Q29=makeQuery(id+"F0.imprint","IMPRINT",FACE,{"disambiguationData":[TD([[makeQuery(id+"F0.imprint","IMPRINT",EDGE,{"disambiguationData":[TD([[subQ4,1.0]])],"derivedFrom":subQ3}),-1.0]])]});}
            var Q30;
            {var subQ3=sQuery(id+"F0.wireOp",EDGE,"E221");var subQ5=sQuery(id+"F0.wireOp",EDGE,"E132.MirrorCS");var subQ8=makeQuery(id+"F0.imprint","INTERSECT",VERTEX,{"derivedFrom":[subQ5,subQ3]});Q30=makeQuery(id+"F0.imprint","IMPRINT",FACE,{"disambiguationData":[TD([[makeQuery(id+"F0.imprint","IMPRINT",EDGE,{"disambiguationData":[TD([[subQ8,1.0]])],"derivedFrom":subQ3}),1.0]])]});}
            var Q31;
            {var subQ1=sQuery(id+"F0.wireOp",EDGE,"E147.MirrorCS");var subQ3=sQuery(id+"F0.wireOp",EDGE,"E221");var subQ4=makeQuery(id+"F0.imprint","INTERSECT",VERTEX,{"derivedFrom":[subQ1,subQ3]});Q31=makeQuery(id+"F0.imprint","IMPRINT",FACE,{"disambiguationData":[TD([[makeQuery(id+"F0.imprint","IMPRINT",EDGE,{"disambiguationData":[TD([[subQ4,1.0]])],"derivedFrom":subQ3}),-1.0]])]});}
            var Q32;
            {var subQ3=sQuery(id+"F0.wireOp",EDGE,"E221");var subQ5=sQuery(id+"F0.wireOp",EDGE,"E147.MirrorCS");var subQ8=makeQuery(id+"F0.imprint","INTERSECT",VERTEX,{"derivedFrom":[subQ5,subQ3]});Q32=makeQuery(id+"F0.imprint","IMPRINT",FACE,{"disambiguationData":[TD([[makeQuery(id+"F0.imprint","IMPRINT",EDGE,{"disambiguationData":[TD([[subQ8,1.0]])],"derivedFrom":subQ3}),1.0]])]});}
            var Q33;
            {var subQ3=sQuery(id+"F0.wireOp",EDGE,"E221");var subQ5=sQuery(id+"F0.wireOp",EDGE,"E155.MirrorCS");var subQ8=makeQuery(id+"F0.imprint","INTERSECT",VERTEX,{"derivedFrom":[subQ5,subQ3]});Q33=makeQuery(id+"F0.imprint","IMPRINT",FACE,{"disambiguationData":[TD([[makeQuery(id+"F0.imprint","IMPRINT",EDGE,{"disambiguationData":[TD([[subQ8,1.0]])],"derivedFrom":subQ3}),1.0]])]});}
            var Q34;
            {var subQ1=sQuery(id+"F0.wireOp",EDGE,"E186.MirrorCS");var subQ3=sQuery(id+"F0.wireOp",EDGE,"E221");var subQ4=makeQuery(id+"F0.imprint","INTERSECT",VERTEX,{"derivedFrom":[subQ1,subQ3]});Q34=makeQuery(id+"F0.imprint","IMPRINT",FACE,{"disambiguationData":[TD([[makeQuery(id+"F0.imprint","IMPRINT",EDGE,{"disambiguationData":[TD([[subQ4,1.0]])],"derivedFrom":subQ3}),-1.0]])]});}
            var Q35;
            {var subQ1=sQuery(id+"F0.wireOp",EDGE,"E186.MirrorCS");var subQ6=sQuery(id+"F0.wireOp",EDGE,"E221");var subQ8=makeQuery(id+"F0.imprint","INTERSECT",VERTEX,{"derivedFrom":[subQ1,subQ6]});Q35=makeQuery(id+"F0.imprint","IMPRINT",FACE,{"disambiguationData":[TD([[makeQuery(id+"F0.imprint","IMPRINT",EDGE,{"disambiguationData":[TD([[subQ8,1.0]])],"derivedFrom":subQ6}),1.0]])]});}
            var Q36;
            {var subQ1=sQuery(id+"F0.wireOp",EDGE,"E131.MirrorCS");var subQ3=sQuery(id+"F0.wireOp",EDGE,"E221");var subQ4=makeQuery(id+"F0.imprint","INTERSECT",VERTEX,{"derivedFrom":[subQ1,subQ3]});Q36=makeQuery(id+"F0.imprint","IMPRINT",FACE,{"disambiguationData":[TD([[makeQuery(id+"F0.imprint","IMPRINT",EDGE,{"disambiguationData":[TD([[subQ4,-1.0]])],"derivedFrom":subQ3}),-1.0]])]});}
            var Q37;
            {var subQ3=sQuery(id+"F0.wireOp",EDGE,"E221");var subQ5=sQuery(id+"F0.wireOp",EDGE,"E131.MirrorCS");var subQ8=makeQuery(id+"F0.imprint","INTERSECT",VERTEX,{"derivedFrom":[subQ5,subQ3]});Q37=makeQuery(id+"F0.imprint","IMPRINT",FACE,{"disambiguationData":[TD([[makeQuery(id+"F0.imprint","IMPRINT",EDGE,{"disambiguationData":[TD([[subQ8,-1.0]])],"derivedFrom":subQ3}),1.0]])]});}
            var Q38;
            {var subQ1=sQuery(id+"F0.wireOp",EDGE,"E155.MirrorCS");var subQ3=sQuery(id+"F0.wireOp",EDGE,"E221");var subQ4=makeQuery(id+"F0.imprint","INTERSECT",VERTEX,{"derivedFrom":[subQ1,subQ3]});Q38=makeQuery(id+"F0.imprint","IMPRINT",FACE,{"disambiguationData":[TD([[makeQuery(id+"F0.imprint","IMPRINT",EDGE,{"disambiguationData":[TD([[subQ4,1.0]])],"derivedFrom":subQ3}),-1.0]])]});}
            var Q39;
            {var subQ1=sQuery(id+"F0.wireOp",EDGE,"E168.MirrorCS");var subQ3=sQuery(id+"F0.wireOp",EDGE,"E221");var subQ4=makeQuery(id+"F0.imprint","INTERSECT",VERTEX,{"derivedFrom":[subQ1,subQ3]});Q39=makeQuery(id+"F0.imprint","IMPRINT",FACE,{"disambiguationData":[TD([[makeQuery(id+"F0.imprint","IMPRINT",EDGE,{"disambiguationData":[TD([[subQ4,1.0]])],"derivedFrom":subQ3}),-1.0]])]});}
            var Q40;
            {var subQ0=sQuery(id+"F0.wireOp",EDGE,"E224");var subQ1=sQuery(id+"F0.wireOp",EDGE,"E217");var subQ2=makeQuery(id+"F0.imprint","INTERSECT",VERTEX,{"disambiguationData":[OD(0.0)],"derivedFrom":[subQ1,subQ0]});Q40=makeQuery(id+"F0.imprint","IMPRINT",FACE,{"disambiguationData":[TD([[makeQuery(id+"F0.imprint","IMPRINT",EDGE,{"disambiguationData":[TD([[subQ2,-1.0]])],"derivedFrom":subQ0}),1.0]])]});}
            var Q41;
            {var subQ0=sQuery(id+"F0.wireOp",EDGE,"E224");var subQ1=sQuery(id+"F0.wireOp",EDGE,"E215");var subQ2=makeQuery(id+"F0.imprint","INTERSECT",VERTEX,{"disambiguationData":[OD(0.0)],"derivedFrom":[subQ1,subQ0]});Q41=makeQuery(id+"F0.imprint","IMPRINT",FACE,{"disambiguationData":[TD([[makeQuery(id+"F0.imprint","IMPRINT",EDGE,{"disambiguationData":[TD([[subQ2,1.0]])],"derivedFrom":subQ0}),1.0]])]});}
            var Q42;
            {var subQ0=sQuery(id+"F0.wireOp",EDGE,"E224");var subQ1=sQuery(id+"F0.wireOp",EDGE,"E214");var subQ2=makeQuery(id+"F0.imprint","INTERSECT",VERTEX,{"disambiguationData":[OD(1.0)],"derivedFrom":[subQ1,subQ0]});Q42=makeQuery(id+"F0.imprint","IMPRINT",FACE,{"disambiguationData":[TD([[makeQuery(id+"F0.imprint","IMPRINT",EDGE,{"disambiguationData":[TD([[subQ2,1.0]])],"derivedFrom":subQ0}),1.0]])]});}
            var Q43;
            {var subQ0=sQuery(id+"F0.wireOp",EDGE,"E224");var subQ1=sQuery(id+"F0.wireOp",EDGE,"E214");var subQ2=makeQuery(id+"F0.imprint","INTERSECT",VERTEX,{"disambiguationData":[OD(1.0)],"derivedFrom":[subQ1,subQ0]});Q43=makeQuery(id+"F0.imprint","IMPRINT",FACE,{"disambiguationData":[TD([[makeQuery(id+"F0.imprint","IMPRINT",EDGE,{"disambiguationData":[TD([[subQ2,-1.0]])],"derivedFrom":subQ0}),1.0]])]});}
            var Q44;
            {var subQ0=sQuery(id+"F0.wireOp",EDGE,"E224");var subQ1=sQuery(id+"F0.wireOp",EDGE,"E216");var subQ2=makeQuery(id+"F0.imprint","INTERSECT",VERTEX,{"disambiguationData":[OD(1.0)],"derivedFrom":[subQ1,subQ0]});Q44=makeQuery(id+"F0.imprint","IMPRINT",FACE,{"disambiguationData":[TD([[makeQuery(id+"F0.imprint","IMPRINT",EDGE,{"disambiguationData":[TD([[subQ2,1.0]])],"derivedFrom":subQ0}),1.0]])]});}
            var Q45;
            {var subQ0=sQuery(id+"F0.wireOp",EDGE,"E224");var subQ1=sQuery(id+"F0.wireOp",EDGE,"E216");var subQ2=makeQuery(id+"F0.imprint","INTERSECT",VERTEX,{"disambiguationData":[OD(1.0)],"derivedFrom":[subQ1,subQ0]});Q45=makeQuery(id+"F0.imprint","IMPRINT",FACE,{"disambiguationData":[TD([[makeQuery(id+"F0.imprint","IMPRINT",EDGE,{"disambiguationData":[TD([[subQ2,-1.0]])],"derivedFrom":subQ0}),1.0]])]});}
            var Q46;
            {var subQ0=sQuery(id+"F0.wireOp",EDGE,"E224");var subQ1=sQuery(id+"F0.wireOp",EDGE,"E217");var subQ2=makeQuery(id+"F0.imprint","INTERSECT",VERTEX,{"disambiguationData":[OD(1.0)],"derivedFrom":[subQ1,subQ0]});Q46=makeQuery(id+"F0.imprint","IMPRINT",FACE,{"disambiguationData":[TD([[makeQuery(id+"F0.imprint","IMPRINT",EDGE,{"disambiguationData":[TD([[subQ2,1.0]])],"derivedFrom":subQ0}),1.0]])]});}
            var Q47;
            {var subQ0=sQuery(id+"F0.wireOp",EDGE,"E224");var subQ1=sQuery(id+"F0.wireOp",EDGE,"E217");var subQ2=makeQuery(id+"F0.imprint","INTERSECT",VERTEX,{"disambiguationData":[OD(1.0)],"derivedFrom":[subQ1,subQ0]});Q47=makeQuery(id+"F0.imprint","IMPRINT",FACE,{"disambiguationData":[TD([[makeQuery(id+"F0.imprint","IMPRINT",EDGE,{"disambiguationData":[TD([[subQ2,-1.0]])],"derivedFrom":subQ0}),1.0]])]});}
            var Q48;
            {var subQ0=sQuery(id+"F0.wireOp",EDGE,"E224");var subQ1=sQuery(id+"F0.wireOp",EDGE,"E215");var subQ2=makeQuery(id+"F0.imprint","INTERSECT",VERTEX,{"disambiguationData":[OD(1.0)],"derivedFrom":[subQ1,subQ0]});Q48=makeQuery(id+"F0.imprint","IMPRINT",FACE,{"disambiguationData":[TD([[makeQuery(id+"F0.imprint","IMPRINT",EDGE,{"disambiguationData":[TD([[subQ2,1.0]])],"derivedFrom":subQ0}),1.0]])]});}
            var Q49;
            {var subQ0=sQuery(id+"F0.wireOp",EDGE,"E224");var subQ1=sQuery(id+"F0.wireOp",EDGE,"E214");var subQ2=makeQuery(id+"F0.imprint","INTERSECT",VERTEX,{"disambiguationData":[OD(0.0)],"derivedFrom":[subQ1,subQ0]});Q49=makeQuery(id+"F0.imprint","IMPRINT",FACE,{"disambiguationData":[TD([[makeQuery(id+"F0.imprint","IMPRINT",EDGE,{"disambiguationData":[TD([[subQ2,1.0]])],"derivedFrom":subQ0}),1.0]])]});}
            var Q50;
            {var subQ0=sQuery(id+"F0.wireOp",EDGE,"E224");var subQ1=sQuery(id+"F0.wireOp",EDGE,"E214");var subQ2=makeQuery(id+"F0.imprint","INTERSECT",VERTEX,{"disambiguationData":[OD(0.0)],"derivedFrom":[subQ1,subQ0]});Q50=makeQuery(id+"F0.imprint","IMPRINT",FACE,{"disambiguationData":[TD([[makeQuery(id+"F0.imprint","IMPRINT",EDGE,{"disambiguationData":[TD([[subQ2,-1.0]])],"derivedFrom":subQ0}),1.0]])]});}
            var Q51;
            {var subQ0=sQuery(id+"F0.wireOp",EDGE,"E224");var subQ1=sQuery(id+"F0.wireOp",EDGE,"E216");var subQ2=makeQuery(id+"F0.imprint","INTERSECT",VERTEX,{"disambiguationData":[OD(0.0)],"derivedFrom":[subQ1,subQ0]});Q51=makeQuery(id+"F0.imprint","IMPRINT",FACE,{"disambiguationData":[TD([[makeQuery(id+"F0.imprint","IMPRINT",EDGE,{"disambiguationData":[TD([[subQ2,1.0]])],"derivedFrom":subQ0}),1.0]])]});}
            var Q52;
            {var subQ0=sQuery(id+"F0.wireOp",EDGE,"E224");var subQ1=sQuery(id+"F0.wireOp",EDGE,"E216");var subQ2=makeQuery(id+"F0.imprint","INTERSECT",VERTEX,{"disambiguationData":[OD(0.0)],"derivedFrom":[subQ1,subQ0]});Q52=makeQuery(id+"F0.imprint","IMPRINT",FACE,{"disambiguationData":[TD([[makeQuery(id+"F0.imprint","IMPRINT",EDGE,{"disambiguationData":[TD([[subQ2,-1.0]])],"derivedFrom":subQ0}),1.0]])]});}
            var Q53;
            {var subQ0=sQuery(id+"F0.wireOp",EDGE,"E224");var subQ1=sQuery(id+"F0.wireOp",EDGE,"E217");var subQ2=makeQuery(id+"F0.imprint","INTERSECT",VERTEX,{"disambiguationData":[OD(0.0)],"derivedFrom":[subQ1,subQ0]});Q53=makeQuery(id+"F0.imprint","IMPRINT",FACE,{"disambiguationData":[TD([[makeQuery(id+"F0.imprint","IMPRINT",EDGE,{"disambiguationData":[TD([[subQ2,1.0]])],"derivedFrom":subQ0}),1.0]])]});}
            var Q54;
            {var subQ1=sQuery(id+"F0.wireOp",EDGE,"E119");var subQ3=sQuery(id+"F0.wireOp",EDGE,"E217");var subQ4=makeQuery(id+"F0.imprint","INTERSECT",VERTEX,{"derivedFrom":[subQ1,subQ3]});Q54=makeQuery(id+"F0.imprint","IMPRINT",FACE,{"disambiguationData":[TD([[makeQuery(id+"F0.imprint","IMPRINT",EDGE,{"disambiguationData":[TD([[subQ4,1.0]])],"derivedFrom":subQ3}),1.0]])]});}
            var Q55;
            {var subQ1=sQuery(id+"F0.wireOp",EDGE,"E118");var subQ3=sQuery(id+"F0.wireOp",EDGE,"E216");var subQ4=makeQuery(id+"F0.imprint","INTERSECT",VERTEX,{"derivedFrom":[subQ1,subQ3]});Q55=makeQuery(id+"F0.imprint","IMPRINT",FACE,{"disambiguationData":[TD([[makeQuery(id+"F0.imprint","IMPRINT",EDGE,{"disambiguationData":[TD([[subQ4,1.0]])],"derivedFrom":subQ3}),1.0]])]});}
            var Q56;
            {var subQ1=sQuery(id+"F0.wireOp",EDGE,"E117");var subQ3=sQuery(id+"F0.wireOp",EDGE,"E214");var subQ4=makeQuery(id+"F0.imprint","INTERSECT",VERTEX,{"derivedFrom":[subQ1,subQ3]});Q56=makeQuery(id+"F0.imprint","IMPRINT",FACE,{"disambiguationData":[TD([[makeQuery(id+"F0.imprint","IMPRINT",EDGE,{"disambiguationData":[TD([[subQ4,1.0]])],"derivedFrom":subQ3}),1.0]])]});}
            var Q57;
            {var subQ1=sQuery(id+"F0.wireOp",EDGE,"E116");var subQ3=sQuery(id+"F0.wireOp",EDGE,"E220");var subQ4=makeQuery(id+"F0.imprint","INTERSECT",VERTEX,{"derivedFrom":[subQ1,subQ3]});Q57=makeQuery(id+"F0.imprint","IMPRINT",FACE,{"disambiguationData":[TD([[makeQuery(id+"F0.imprint","IMPRINT",EDGE,{"disambiguationData":[TD([[subQ4,1.0]])],"derivedFrom":subQ3}),1.0]])]});}
            var Q58;
            {var subQ1=sQuery(id+"F0.wireOp",EDGE,"E122");var subQ3=sQuery(id+"F0.wireOp",EDGE,"E218");var subQ4=makeQuery(id+"F0.imprint","INTERSECT",VERTEX,{"derivedFrom":[subQ1,subQ3]});Q58=makeQuery(id+"F0.imprint","IMPRINT",FACE,{"disambiguationData":[TD([[makeQuery(id+"F0.imprint","IMPRINT",EDGE,{"disambiguationData":[TD([[subQ4,1.0]])],"derivedFrom":subQ3}),1.0]])]});}
            var Q59;
            {var subQ1=sQuery(id+"F0.wireOp",EDGE,"E121");var subQ3=sQuery(id+"F0.wireOp",EDGE,"E219");var subQ4=makeQuery(id+"F0.imprint","INTERSECT",VERTEX,{"derivedFrom":[subQ1,subQ3]});Q59=makeQuery(id+"F0.imprint","IMPRINT",FACE,{"disambiguationData":[TD([[makeQuery(id+"F0.imprint","IMPRINT",EDGE,{"disambiguationData":[TD([[subQ4,1.0]])],"derivedFrom":subQ3}),1.0]])]});}
            var Q60;
            {var subQ1=sQuery(id+"F0.wireOp",EDGE,"E120");var subQ3=sQuery(id+"F0.wireOp",EDGE,"E215");var subQ4=makeQuery(id+"F0.imprint","INTERSECT",VERTEX,{"derivedFrom":[subQ1,subQ3]});Q60=makeQuery(id+"F0.imprint","IMPRINT",FACE,{"disambiguationData":[TD([[makeQuery(id+"F0.imprint","IMPRINT",EDGE,{"disambiguationData":[TD([[subQ4,1.0]])],"derivedFrom":subQ3}),1.0]])]});}
            var Q61;
            {var subQ1=sQuery(id+"F0.wireOp",EDGE,"E134.MirrorCS");var subQ3=sQuery(id+"F0.wireOp",EDGE,"E144.MirrorCS");var subQ4=makeQuery(id+"F0.imprint","INTERSECT",VERTEX,{"derivedFrom":[subQ1,subQ3]});Q61=makeQuery(id+"F0.imprint","IMPRINT",FACE,{"disambiguationData":[TD([[makeQuery(id+"F0.imprint","IMPRINT",EDGE,{"disambiguationData":[TD([[subQ4,1.0]])],"derivedFrom":subQ1}),1.0]])]});}
            var Q62;
            {var subQ1=sQuery(id+"F0.wireOp",EDGE,"E147.MirrorCS");var subQ3=sQuery(id+"F0.wireOp",EDGE,"E221");var subQ4=makeQuery(id+"F0.imprint","INTERSECT",VERTEX,{"derivedFrom":[subQ1,subQ3]});Q62=makeQuery(id+"F0.imprint","IMPRINT",FACE,{"disambiguationData":[TD([[makeQuery(id+"F0.imprint","IMPRINT",EDGE,{"disambiguationData":[TD([[subQ4,-1.0]])],"derivedFrom":subQ3}),1.0]])]});}
            var Q63;
            {var subQ1=sQuery(id+"F0.wireOp",EDGE,"E132.MirrorCS");var subQ3=sQuery(id+"F0.wireOp",EDGE,"E221");var subQ4=makeQuery(id+"F0.imprint","INTERSECT",VERTEX,{"derivedFrom":[subQ1,subQ3]});Q63=makeQuery(id+"F0.imprint","IMPRINT",FACE,{"disambiguationData":[TD([[makeQuery(id+"F0.imprint","IMPRINT",EDGE,{"disambiguationData":[TD([[subQ4,-1.0]])],"derivedFrom":subQ3}),1.0]])]});}
            var Q64;
            {var subQ1=sQuery(id+"F0.wireOp",EDGE,"E131.MirrorCS");var subQ3=sQuery(id+"F0.wireOp",EDGE,"E221");var subQ4=makeQuery(id+"F0.imprint","INTERSECT",VERTEX,{"derivedFrom":[subQ1,subQ3]});Q64=makeQuery(id+"F0.imprint","IMPRINT",FACE,{"disambiguationData":[TD([[makeQuery(id+"F0.imprint","IMPRINT",EDGE,{"disambiguationData":[TD([[subQ4,1.0]])],"derivedFrom":subQ3}),1.0]])]});}
            var Q65;
            {var subQ1=sQuery(id+"F0.wireOp",EDGE,"E196.MirrorCS");var subQ3=sQuery(id+"F0.wireOp",EDGE,"E221");var subQ4=makeQuery(id+"F0.imprint","INTERSECT",VERTEX,{"derivedFrom":[subQ1,subQ3]});Q65=makeQuery(id+"F0.imprint","IMPRINT",FACE,{"disambiguationData":[TD([[makeQuery(id+"F0.imprint","IMPRINT",EDGE,{"disambiguationData":[TD([[subQ4,1.0]])],"derivedFrom":subQ3}),1.0]])]});}
            var Q66;
            {var subQ1=sQuery(id+"F0.wireOp",EDGE,"E155.MirrorCS");var subQ3=sQuery(id+"F0.wireOp",EDGE,"E221");var subQ4=makeQuery(id+"F0.imprint","INTERSECT",VERTEX,{"derivedFrom":[subQ1,subQ3]});Q66=makeQuery(id+"F0.imprint","IMPRINT",FACE,{"disambiguationData":[TD([[makeQuery(id+"F0.imprint","IMPRINT",EDGE,{"disambiguationData":[TD([[subQ4,-1.0]])],"derivedFrom":subQ3}),1.0]])]});}
            var Q67;
            {var subQ1=sQuery(id+"F0.wireOp",EDGE,"E186.MirrorCS");var subQ3=sQuery(id+"F0.wireOp",EDGE,"E221");var subQ4=makeQuery(id+"F0.imprint","INTERSECT",VERTEX,{"derivedFrom":[subQ1,subQ3]});Q67=makeQuery(id+"F0.imprint","IMPRINT",FACE,{"disambiguationData":[TD([[makeQuery(id+"F0.imprint","IMPRINT",EDGE,{"disambiguationData":[TD([[subQ4,-1.0]])],"derivedFrom":subQ3}),1.0]])]});}
            var Q68;
            {var subQ1=sQuery(id+"F0.wireOp",EDGE,"E168.MirrorCS");var subQ3=sQuery(id+"F0.wireOp",EDGE,"E221");var subQ4=makeQuery(id+"F0.imprint","INTERSECT",VERTEX,{"derivedFrom":[subQ1,subQ3]});Q68=makeQuery(id+"F0.imprint","IMPRINT",FACE,{"disambiguationData":[TD([[makeQuery(id+"F0.imprint","IMPRINT",EDGE,{"disambiguationData":[TD([[subQ4,-1.0]])],"derivedFrom":subQ3}),1.0]])]});}
            var Q69;
            {var subQ3=sQuery(id+"F0.wireOp",EDGE,"E221");var subQ5=sQuery(id+"F0.wireOp",EDGE,"E168.MirrorCS");var subQ8=makeQuery(id+"F0.imprint","INTERSECT",VERTEX,{"derivedFrom":[subQ5,subQ3]});Q69=makeQuery(id+"F0.imprint","IMPRINT",FACE,{"disambiguationData":[TD([[makeQuery(id+"F0.imprint","IMPRINT",EDGE,{"disambiguationData":[TD([[subQ8,1.0]])],"derivedFrom":subQ3}),1.0]])]});}
            var Q70;
            {var subQ1=sQuery(id+"F0.wireOp",EDGE,"E189.MirrorCS");var subQ3=sQuery(id+"F0.wireOp",EDGE,"E212.MirrorCS");var subQ4=makeQuery(id+"F0.imprint","INTERSECT",VERTEX,{"derivedFrom":[subQ1,subQ3]});Q70=makeQuery(id+"F0.imprint","IMPRINT",FACE,{"disambiguationData":[TD([[makeQuery(id+"F0.imprint","IMPRINT",EDGE,{"disambiguationData":[TD([[subQ4,1.0]])],"derivedFrom":subQ1}),-1.0]])]});}
            var Q71;
            {var subQ1=sQuery(id+"F0.wireOp",EDGE,"E130.MirrorCS");var subQ3=sQuery(id+"F0.wireOp",EDGE,"E197.MirrorCS");var subQ4=makeQuery(id+"F0.imprint","INTERSECT",VERTEX,{"derivedFrom":[subQ1,subQ3]});Q71=makeQuery(id+"F0.imprint","IMPRINT",FACE,{"disambiguationData":[TD([[makeQuery(id+"F0.imprint","IMPRINT",EDGE,{"disambiguationData":[TD([[subQ4,-1.0]])],"derivedFrom":subQ1}),1.0]])]});}
            var Q72;
            {var subQ1=sQuery(id+"F0.wireOp",EDGE,"E148.MirrorCS");var subQ3=sQuery(id+"F0.wireOp",EDGE,"E160.MirrorCS");var subQ4=makeQuery(id+"F0.imprint","INTERSECT",VERTEX,{"derivedFrom":[subQ1,subQ3]});Q72=makeQuery(id+"F0.imprint","IMPRINT",FACE,{"disambiguationData":[TD([[makeQuery(id+"F0.imprint","IMPRINT",EDGE,{"disambiguationData":[TD([[subQ4,1.0]])],"derivedFrom":subQ1}),1.0]])]});}
            var Q73;
            {var subQ1=sQuery(id+"F0.wireOp",EDGE,"E159.MirrorCS");var subQ3=sQuery(id+"F0.wireOp",EDGE,"E172.MirrorCS");var subQ4=makeQuery(id+"F0.imprint","INTERSECT",VERTEX,{"derivedFrom":[subQ1,subQ3]});Q73=makeQuery(id+"F0.imprint","IMPRINT",FACE,{"disambiguationData":[TD([[makeQuery(id+"F0.imprint","IMPRINT",EDGE,{"disambiguationData":[TD([[subQ4,1.0]])],"derivedFrom":subQ1}),1.0]])]});}
            var Q74;
            {var subQ1=sQuery(id+"F0.wireOp",EDGE,"E185.MirrorCS");var subQ3=sQuery(id+"F0.wireOp",EDGE,"E201.MirrorCS");var subQ4=makeQuery(id+"F0.imprint","INTERSECT",VERTEX,{"derivedFrom":[subQ1,subQ3]});Q74=makeQuery(id+"F0.imprint","IMPRINT",FACE,{"disambiguationData":[TD([[makeQuery(id+"F0.imprint","IMPRINT",EDGE,{"disambiguationData":[TD([[subQ4,1.0]])],"derivedFrom":subQ1}),1.0]])]});}
            var Q75;
            {var subQ1=sQuery(id+"F0.wireOp",EDGE,"E169.MirrorCS");var subQ3=sQuery(id+"F0.wireOp",EDGE,"E181.MirrorCS");var subQ4=makeQuery(id+"F0.imprint","INTERSECT",VERTEX,{"derivedFrom":[subQ1,subQ3]});Q75=makeQuery(id+"F0.imprint","IMPRINT",FACE,{"disambiguationData":[TD([[makeQuery(id+"F0.imprint","IMPRINT",EDGE,{"disambiguationData":[TD([[subQ4,1.0]])],"derivedFrom":subQ1}),1.0]])]});}
            extrude(context, id + "F1", {"entities" : qUnion([Q0, Q1, Q2, Q3, Q4, Q5, Q6, Q7, Q8, Q9, Q10, Q11, Q12, Q13, Q14, Q15, Q16, Q17, Q18, Q19, Q20, Q21, Q22, Q23, Q24, Q25, Q26, Q27, Q28, Q29, Q30, Q31, Q32, Q33, Q34, Q35, Q36, Q37, Q38, Q39, Q40, Q41, Q42, Q43, Q44, Q45, Q46, Q47, Q48, Q49, Q50, Q51, Q52, Q53, Q54, Q55, Q56, Q57, Q58, Q59, Q60, Q61, Q62, Q63, Q64, Q65, Q66, Q67, Q68, Q69, Q70, Q71, Q72, Q73, Q74, Q75]), "depth" : 5 * mm, "offsetDistance" : 25 * mm});
        }
    });
